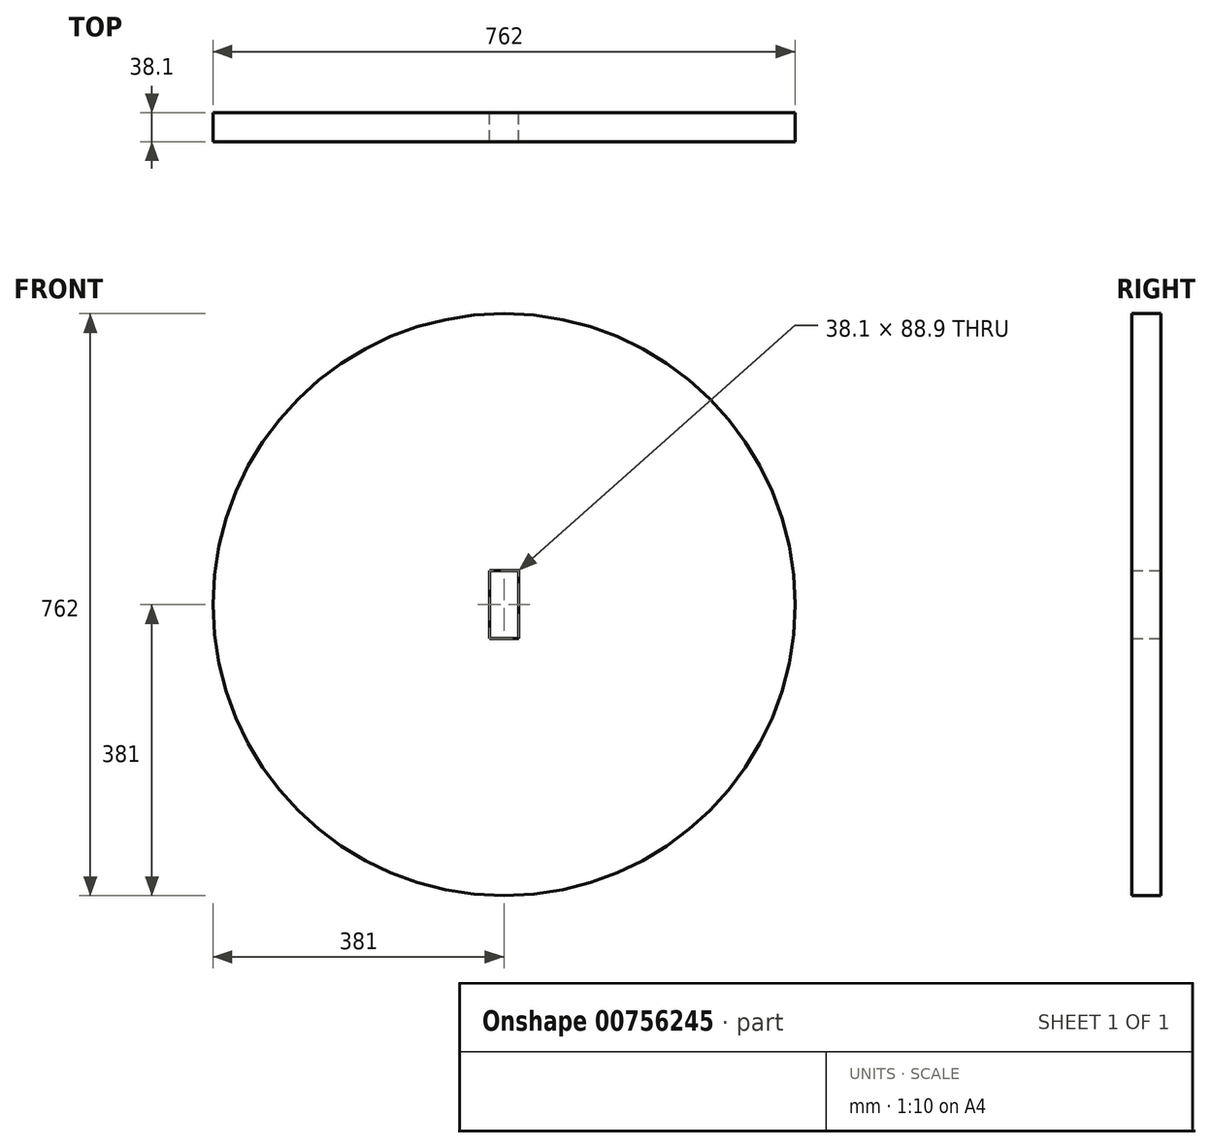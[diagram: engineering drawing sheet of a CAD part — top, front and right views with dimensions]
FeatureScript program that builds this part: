
annotation { "Feature Type Name" : "Feature", "Feature Type Description" : "" }
export const myFeature = defineFeature(function(context is Context, id is Id, definition is map)
    precondition{}
    {
        {
            var Q0;
            Q0=qCreatedBy(makeId("Front.planeOp"),FACE);
            var sketch = newSketch(context, id + "F0", { "sketchPlane" : qUnion([Q0])});
            skCircle(sketch, "E0", {"center": v(0, 0) * mm, "radius": 381 * mm});
            skLineSegment(sketch, "E1.bottom", {"start": v(-19.05, 44.45) * mm, "end": v(19.05, 44.45) * mm});
            skLineSegment(sketch, "E1.top", {"start": v(-19.05, -44.45) * mm, "end": v(19.05, -44.45) * mm});
            skLineSegment(sketch, "E1.left", {"start": v(-19.05, 44.45) * mm, "end": v(-19.05, -44.45) * mm});
            skLineSegment(sketch, "E1.right", {"start": v(19.05, 44.45) * mm, "end": v(19.05, -44.45) * mm});
            skSolve(sketch);
        }
        {
            var Q0;
            Q0=makeQuery(id+"F0.imprint","IMPRINT",FACE,{"disambiguationData":[TD([[makeQuery(id+"F0.imprint","IMPRINT",EDGE,{"derivedFrom":sQuery(id+"F0.wireOp",EDGE,"E0")}),1.0]])]});
            extrude(context, id + "F1", {"entities" : qUnion([Q0]), "endBound" : BoundingType.SYMMETRIC, "depth" : 38.1 * mm, "offsetDistance" : 25.4 * mm});
        }
    });
